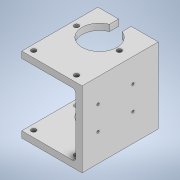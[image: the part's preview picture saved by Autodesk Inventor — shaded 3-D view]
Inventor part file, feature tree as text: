
AUTODESK INVENTOR PART (.ipt)
format: ipt  version: 2022 (Build 260153000, 153)  size: 178,688 bytes
history: native  units: mm
features: sketch x6, extrude x3, hole x3, other x1, fillet x1
ambient origin geometry x8: Origin, YZ Plane, XZ Plane, XY Plane, X Axis, Y Axis, Z Axis, Center Point
bodies: Body1 (feature_tree)
feature tree (14):
  other  "ソリッド1"
  extrude  "押し出し1"  Depth=48.0mm
  extrude  "押し出し2"  Depth=38.0mm
  hole  "穴1"  [1 undecoded]
  hole  "穴2"  [1 undecoded]
  hole  "穴4"  [1 undecoded]
  fillet  "フィレット1"  Radius=4.0mm
  sketch  "スケッチ1"
  sketch  "スケッチ2"
  sketch  "スケッチ3"
  sketch  "スケッチ4"
  sketch  "スケッチ6"
  extrude  "押し出し3"  Depth=100.0mm TaperAngle=0.0deg
  sketch  "スケッチ7"
note: 3 required parameter values undecoded (feature->parameter linkage not recoverable at this tier; creation-order binding heuristic only, values carry confidence <= 0.55)
